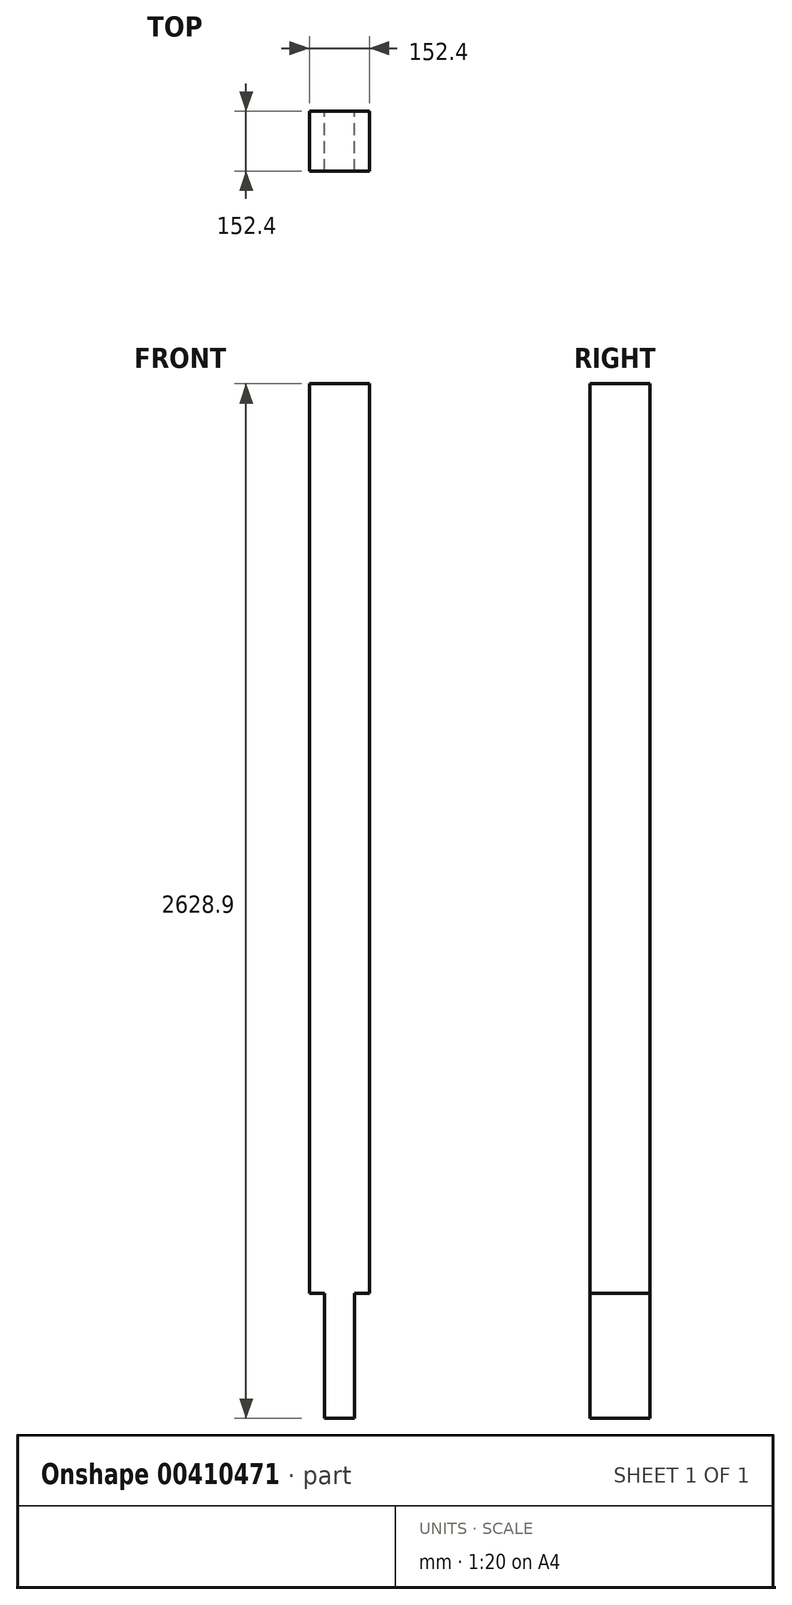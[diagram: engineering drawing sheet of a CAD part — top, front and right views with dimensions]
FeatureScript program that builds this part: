
annotation { "Feature Type Name" : "Feature", "Feature Type Description" : "" }
export const myFeature = defineFeature(function(context is Context, id is Id, definition is map)
    precondition{}
    {
        {
            var Q0;
            Q0=qCreatedBy(makeId("Front.planeOp"),FACE);
            var sketch = newSketch(context, id + "F0", { "sketchPlane" : qUnion([Q0])});
            skLineSegment(sketch, "E0.bottom", {"start": v(-76.2, 1200.15) * mm, "end": v(76.2, 1200.15) * mm});
            skLineSegment(sketch, "E0.top", {"start": v(-76.2, -1200.15) * mm, "end": v(76.2, -1200.15) * mm});
            skLineSegment(sketch, "E0.left", {"start": v(-76.2, 1200.15) * mm, "end": v(-76.2, -1200.15) * mm});
            skLineSegment(sketch, "E0.right", {"start": v(76.2, 1200.15) * mm, "end": v(76.2, -1200.15) * mm});
            skPoint(sketch, "E0.middle", {"position": v(0, 0) * mm});
            skLineSegment(sketch, "E1", {"start": v(-76.2, 1111.25) * mm, "end": v(88.9, 1111.25) * mm});
            skPoint(sketch, "E2.middle", {"position": v(0, 1092.2) * mm});
            skLineSegment(sketch, "E3.bottom", {"start": v(6.35, 1111.25) * mm, "end": v(44.45, 1111.25) * mm});
            skLineSegment(sketch, "E3.top", {"start": v(6.35, 1200.15) * mm, "end": v(44.45, 1200.15) * mm});
            skLineSegment(sketch, "E3.left", {"start": v(6.35, 1111.25) * mm, "end": v(6.35, 1200.15) * mm});
            skLineSegment(sketch, "E3.right", {"start": v(44.45, 1111.25) * mm, "end": v(44.45, 1200.15) * mm});
            skSolve(sketch);
        }
        {
            var Q0;
            {var subQ1=sQuery(id+"F0.wireOp",EDGE,"E0.top");Q0=makeQuery(id+"F0.imprint","IMPRINT",FACE,{"disambiguationData":[TD([[makeQuery(id+"F0.imprint","IMPRINT",EDGE,{"derivedFrom":subQ1}),1.0]])]});}
            var Q1;
            Q1=makeQuery(id+"F0.imprint","IMPRINT",FACE,{"disambiguationData":[TD([[makeQuery(id+"F0.imprint","IMPRINT",EDGE,{"derivedFrom":sQuery(id+"F0.wireOp",EDGE,"OlOpib3l-DV6w-VdAR-WjI2-fuE5ldOcum9m.bottom")}),1.0]])]});
            var Q2;
            Q2=makeQuery(id+"F0.imprint","IMPRINT",FACE,{"disambiguationData":[TD([[makeQuery(id+"F0.imprint","IMPRINT",EDGE,{"derivedFrom":sQuery(id+"F0.wireOp",EDGE,"E2.bottom")}),1.0]])]});
            var Q3;
            Q3=makeQuery(id+"F0.imprint","IMPRINT",FACE,{"disambiguationData":[TD([[makeQuery(id+"F0.imprint","IMPRINT",EDGE,{"derivedFrom":sQuery(id+"F0.wireOp",EDGE,"E3.bottom")}),1.0]])]});
            extrude(context, id + "F1", {"entities" : qUnion([Q0, Q1, Q2, Q3]), "depth" : 152.4 * mm, "symmetric" : true});
        }
        {
            var Q0;
            Q0=makeQuery(id+"F1.opExtrude","SWEPT_FACE",FACE,{"disambiguationData":[OSD([sQuery(id+"F0.wireOp",EDGE,"E0.top")])]});
            var sketch = newSketch(context, id + "F2", { "sketchPlane" : qUnion([Q0])});
            skLineSegment(sketch, "E4.bottom", {"start": v(-38.1, 76.2) * mm, "end": v(38.1, 76.2) * mm});
            skLineSegment(sketch, "E4.top", {"start": v(-38.1, -76.2) * mm, "end": v(38.1, -76.2) * mm});
            skLineSegment(sketch, "E4.left", {"start": v(-38.1, 76.2) * mm, "end": v(-38.1, -76.2) * mm});
            skLineSegment(sketch, "E4.right", {"start": v(38.1, 76.2) * mm, "end": v(38.1, -76.2) * mm});
            skSolve(sketch);
        }
        {
            var Q0;
            Q0 = qSketchRegion(id + "F2", true);
            extrude(context, id + "F3", {"entities" : qUnion([Q0]), "operationType" : NewBodyOperationType.ADD, "depth" : 317.5 * mm, "offsetDistance" : 25.4 * mm});
        }
    });
